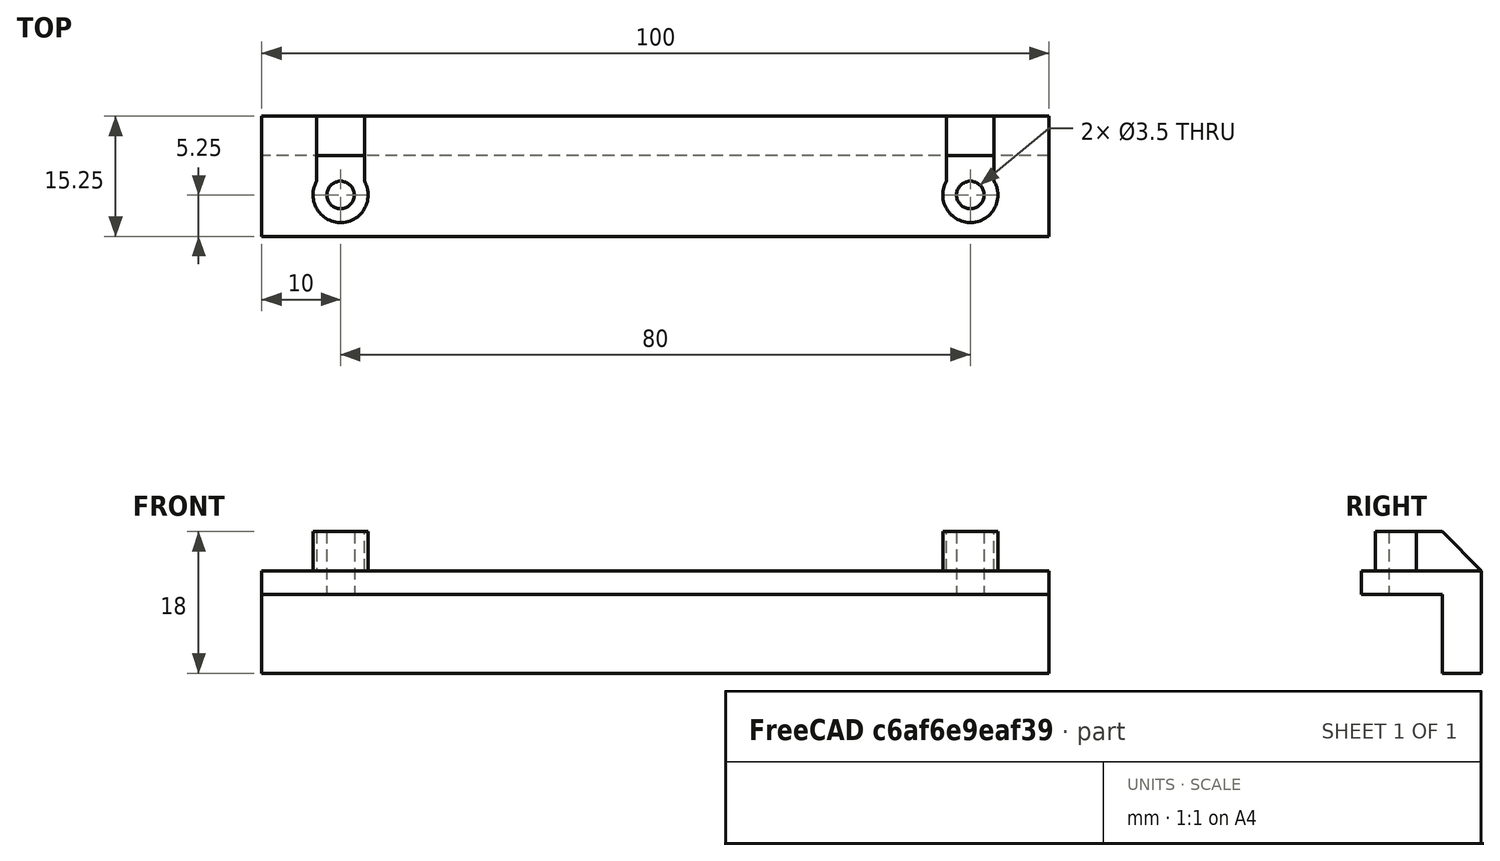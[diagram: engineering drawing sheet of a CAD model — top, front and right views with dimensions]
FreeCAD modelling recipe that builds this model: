
FCSTD DOCUMENT  (FreeCAD 0.19R24276 (Git))
Label: hole_jig
License: All rights reserved
LicenseURL: http://en.wikipedia.org/wiki/All_rights_reserved
objects: TechDraw::DrawProjGroupItem×9, TechDraw::DrawViewDimension×8, Sketcher::SketchObject×4, PartDesign::Pad×4, Spreadsheet::Sheet×1, PartDesign::Chamfer×1, PartDesign::Body×1, TechDraw::DrawSVGTemplate×1, TechDraw::DrawProjGroup×1, TechDraw::DrawPage×1
note: 15 computed .brp shape members not serialized (recipe doc carries the construction recipe); baked Part::Feature solids carry a one-line shape summary decoded from their .brp

FEATURE [Spreadsheet::Sheet] Spreadsheet  label="parameters"
  cells = A1=table_thickness; B1(table_thickness)=10; A2=gap; B2(gap)=0.25; A3=hole_separation; B3(hole_separation)=80; A4=hole_height; B4(hole_height)=5; A5=hole_diameter; B5(hole_diameter)=3; A6=jig_top_thickness; B6(jig_top_thickness)=3; A7=jig_side_thickness; B7(jig_side_thickness)=5; A8=wall; B8(wall)=2
FEATURE [Sketcher::SketchObject] Sketch
  FullyConstrained = true
  MapMode = 5
  Support = -> [XY_Plane]
  expr: Constraints[12] = <<parameters>>.hole_separation / 2
  expr: Constraints[13] = <<parameters>>.table_thickness / 2 + <<parameters>>.gap
  expr: Constraints[7] = <<parameters>>.table_thickness + <<parameters>>.gap + <<parameters>>.jig_side_thickness
  expr: Constraints[8] = <<parameters>>.hole_separation + <<parameters>>.table_thickness * 2
  expr: Constraints[11] = <<parameters>>.hole_separation / 2
  expr: Constraints[9] = <<parameters>>.hole_diameter / 2 + <<parameters>>.gap
  sketch-geometry (6):
    g0: LineSegment StartX=-50 StartY=0 StartZ=0 EndX=50 EndY=0 EndZ=0
    g1: LineSegment StartX=50 StartY=0 StartZ=0 EndX=50 EndY=-15.25 EndZ=0
    g2: LineSegment StartX=50 StartY=-15.25 StartZ=0 EndX=-50 EndY=-15.25 EndZ=0
    g3: LineSegment StartX=-50 StartY=-15.25 StartZ=0 EndX=-50 EndY=0 EndZ=0
    g4: Circle CenterX=-40 CenterY=-10 CenterZ=0 NormalX=0 NormalY=0 NormalZ=1 AngleXU=0 Radius=1.75
    g5: Circle CenterX=40 CenterY=-10 CenterZ=0 NormalX=0 NormalY=0 NormalZ=1 AngleXU=0 Radius=1.75
  constraints (17):
    c: Coincident(g0,g1)
    c: Coincident(g1,g2)
    c: Coincident(g2,g3)
    c: Coincident(g3,g0)
    c: Horizontal(g0)
    c: Vertical(g1)
    c: Vertical(g3)
    c: DistanceY(g1,g1) = 15.25
    c: DistanceX(g0,g0) = 100
    c: Radius(g4) = 1.75
    c: Equal(g4,g5)
    c: DistanceX(g4,g-1) = 40
    c: DistanceX(g-1,g5) = 40
    c: DistanceY(g2,g4) = 5.25
    c: Horizontal(g5,g4)
    c: Symmetric(g2,g1,g-2)
    c: PointOnObject(g0,g-1)
FEATURE [PartDesign::Pad] Pad
  Direction = (1,1,1)
  Length = 3
  Length2 = 100
  Profile = -> Sketch
  Type = 0
  expr: Length = <<parameters>>.jig_top_thickness
FEATURE [Sketcher::SketchObject] Sketch001
  ExternalGeometry = -> [Pad]
  FullyConstrained = true
  MapMode = 5
  Placement = pos=(0,0,0) rot=(1,0,0;3.14159rad)
  Support = -> [Pad]
  expr: Constraints[10] = <<parameters>>.jig_side_thickness
  sketch-geometry (4):
    g0: LineSegment StartX=-50 StartY=0 StartZ=0 EndX=50 EndY=0 EndZ=0
    g1: LineSegment StartX=50 StartY=0 StartZ=0 EndX=50 EndY=5 EndZ=0
    g2: LineSegment StartX=50 StartY=5 StartZ=0 EndX=-50 EndY=5 EndZ=0
    g3: LineSegment StartX=-50 StartY=5 StartZ=0 EndX=-50 EndY=0 EndZ=0
  constraints (11):
    c: Coincident(g0,g1)
    c: Coincident(g1,g2)
    c: Coincident(g2,g3)
    c: Coincident(g3,g0)
    c: Horizontal(g0)
    c: Horizontal(g2)
    c: Vertical(g1)
    c: Vertical(g3)
    c: Coincident(g0,g-3)
    c: PointOnObject(g1,g-4)
    c: DistanceY(g1,g1) = 5
FEATURE [PartDesign::Pad] Pad001
  BaseFeature = -> Pad
  Direction = (1,1,1)
  Length = 10
  Length2 = 100
  Profile = -> Sketch001
  Type = 0
  expr: Length = <<parameters>>.jig_side_thickness * 2
FEATURE [Sketcher::SketchObject] Sketch002
  ExternalGeometry = -> [Pad001]
  FullyConstrained = true
  MapMode = 5
  Placement = pos=(0,0,3) rot=(0,0,1;0rad)
  Support = -> [Pad001]
  expr: Constraints[4] = <<parameters>>.hole_diameter / 2 + <<parameters>>.gap
  expr: Constraints[6] = <<parameters>>.hole_diameter / 2 + <<parameters>>.wall
  sketch-geometry (4):
    g0: Circle CenterX=-40 CenterY=-10 CenterZ=0 NormalX=0 NormalY=0 NormalZ=1 AngleXU=0 Radius=1.75
    g1: Circle CenterX=-40 CenterY=-10 CenterZ=0 NormalX=0 NormalY=0 NormalZ=1 AngleXU=0 Radius=3.5
    g2: Circle CenterX=40 CenterY=-10 CenterZ=0 NormalX=0 NormalY=0 NormalZ=1 AngleXU=0 Radius=1.75
    g3: Circle CenterX=40 CenterY=-10 CenterZ=0 NormalX=0 NormalY=0 NormalZ=1 AngleXU=0 Radius=3.5
  constraints (8):
    c: Coincident(g0,g-3)
    c: Coincident(g1,g0)
    c: Coincident(g2,g-4)
    c: Coincident(g3,g2)
    c: Radius(g0) = 1.75
    c: Equal(g0,g2)
    c: Radius(g1) = 3.5
    c: Equal(g1,g3)
FEATURE [PartDesign::Pad] Pad002
  BaseFeature = -> Pad001
  Direction = (1,1,1)
  Length = 5
  Length2 = 100
  Profile = -> Sketch002
  Type = 0
  expr: Length = <<parameters>>.hole_height
FEATURE [Sketcher::SketchObject] Sketch003
  ExternalGeometry = -> [Pad002]
  FullyConstrained = true
  MapMode = 5
  Placement = pos=(0,0,8) rot=(0,0,1;0rad)
  Support = -> [Pad002]
  sketch-geometry (8):
    g0: LineSegment StartX=-43.0311 StartY=0 StartZ=0 EndX=-36.9689 EndY=0 EndZ=0
    g1: LineSegment StartX=-36.9689 StartY=0 StartZ=0 EndX=-36.9689 EndY=-8.25 EndZ=0
    g2: LineSegment StartX=-36.9689 StartY=-8.25 StartZ=0 EndX=-43.0311 EndY=-8.25 EndZ=0
    g3: LineSegment StartX=-43.0311 StartY=-8.25 StartZ=0 EndX=-43.0311 EndY=0 EndZ=0
    g4: LineSegment StartX=36.9689 StartY=0 StartZ=0 EndX=43.0311 EndY=0 EndZ=0
    g5: LineSegment StartX=43.0311 StartY=0 StartZ=0 EndX=43.0311 EndY=-8.25 EndZ=0
    g6: LineSegment StartX=43.0311 StartY=-8.25 StartZ=0 EndX=36.9689 EndY=-8.25 EndZ=0
    g7: LineSegment StartX=36.9689 StartY=-8.25 StartZ=0 EndX=36.9689 EndY=0 EndZ=0
  constraints (24):
    c: Coincident(g0,g1)
    c: Coincident(g1,g2)
    c: Coincident(g2,g3)
    c: Coincident(g3,g0)
    c: Horizontal(g0)
    c: Horizontal(g2)
    c: Vertical(g1)
    c: Vertical(g3)
    c: PointOnObject(g0,g-3)
    c: PointOnObject(g1,g-4)
    c: Coincident(g4,g5)
    c: Coincident(g5,g6)
    c: Coincident(g6,g7)
    c: Coincident(g7,g4)
    c: Horizontal(g4)
    c: Horizontal(g6)
    c: Vertical(g5)
    c: Vertical(g7)
    c: PointOnObject(g4,g-3)
    c: PointOnObject(g5,g-6)
    c: PointOnObject(g6,g-6)
    c: Tangent(g6,g-7)
    c: PointOnObject(g2,g-4)
    c: Tangent(g2,g-5)
FEATURE [PartDesign::Pad] Pad003
  BaseFeature = -> Pad002
  Direction = (1,1,1)
  Length = 5
  Length2 = 100
  Profile = -> Sketch003
  Refine = true
  Reversed = true
  Type = 0
  expr: Length = <<parameters>>.hole_height
FEATURE [PartDesign::Chamfer] Chamfer
  Angle = 45
  Base = -> Pad003 [Edge41,Edge42]
  BaseFeature = -> Pad003
  ChamferType = 0
  FlipDirection = false
  Size = 5
  Size2 = 1
  SupportTransform = false
  expr: Size = <<parameters>>.hole_height
FEATURE [PartDesign::Body] Body
  Group = -> [Sketch,Pad,Sketch001,Pad001,Sketch002,Pad002,Sketch003,Pad003,Chamfer]
  Origin = -> Origin
  Tip = -> Chamfer
FEATURE [TechDraw::DrawSVGTemplate] Template_Chamfer
  Height = 210
  Orientation = 1
  Width = 297
FEATURE [TechDraw::DrawProjGroupItem] ProjItem  label="Front"
  CoarseView = false
  Direction = (0,-1,0)
  Focus = 100
  HardHidden = false
  IsoCount = 0
  IsoHidden = false
  IsoVisible = false
  LockPosition = true
  Perspective = false
  Rotation = 0
  RotationVector = (1,0,0)
  Scale = 0.5
  ScaleType = 2
  SeamHidden = false
  SeamVisible = true
  SmoothHidden = false
  SmoothVisible = true
  Source = -> [Chamfer]
  Type = 0
  X = 0
  XDirection = (1,0,0)
  Y = 0
FEATURE [TechDraw::DrawProjGroupItem] ProjItem001  label="Right"
  CoarseView = false
  Direction = (1,-1e-16,0)
  Focus = 100
  HardHidden = false
  IsoCount = 0
  IsoHidden = false
  IsoVisible = false
  LockPosition = false
  Perspective = false
  Rotation = 0
  RotationVector = (1,0,0)
  Scale = 0.5
  ScaleType = 2
  SeamHidden = false
  SeamVisible = true
  SmoothHidden = false
  SmoothVisible = true
  Source = -> [Chamfer]
  Type = 2
  X = -43.8125
  XDirection = (1e-16,1,0)
  Y = 0
FEATURE [TechDraw::DrawProjGroupItem] ProjItem002  label="Top"
  CoarseView = false
  Direction = (0,0,1)
  Focus = 100
  HardHidden = false
  IsoCount = 0
  IsoHidden = false
  IsoVisible = false
  LockPosition = false
  Perspective = false
  Rotation = 0
  RotationVector = (1,0,0)
  Scale = 0.5
  ScaleType = 2
  SeamHidden = false
  SeamVisible = true
  SmoothHidden = false
  SmoothVisible = true
  Source = -> [Chamfer]
  Type = 4
  X = 0
  XDirection = (1,0,0)
  Y = -86.1875
FEATURE [TechDraw::DrawProjGroupItem] ProjItem003  label="Left"
  CoarseView = false
  Direction = (-1,-1e-16,0)
  Focus = 100
  HardHidden = false
  IsoCount = 0
  IsoHidden = false
  IsoVisible = false
  LockPosition = false
  Perspective = false
  Rotation = 0
  RotationVector = (1,0,0)
  Scale = 0.5
  ScaleType = 2
  SeamHidden = false
  SeamVisible = true
  SmoothHidden = false
  SmoothVisible = true
  Source = -> [Chamfer]
  Type = 1
  X = 43.8125
  XDirection = (1e-16,-1,0)
  Y = 0
FEATURE [TechDraw::DrawProjGroupItem] ProjItem004  label="Bottom"
  CoarseView = false
  Direction = (0,0,-1)
  Focus = 100
  HardHidden = false
  IsoCount = 0
  IsoHidden = false
  IsoVisible = false
  LockPosition = false
  Perspective = false
  Rotation = 0
  RotationVector = (1,0,0)
  Scale = 0.5
  ScaleType = 2
  SeamHidden = false
  SeamVisible = true
  SmoothHidden = false
  SmoothVisible = true
  Source = -> [Chamfer]
  Type = 5
  X = 0
  XDirection = (1,0,0)
  Y = 43.8125
FEATURE [TechDraw::DrawProjGroupItem] ProjItem005  label="FrontBottomLeft"
  CoarseView = false
  Direction = (-0.57735,-0.57735,-0.57735)
  Focus = 100
  HardHidden = false
  IsoCount = 0
  IsoHidden = false
  IsoVisible = false
  LockPosition = false
  Perspective = false
  Rotation = 0
  RotationVector = (1,0,0)
  Scale = 0.5
  ScaleType = 2
  SeamHidden = false
  SeamVisible = true
  SmoothHidden = false
  SmoothVisible = true
  Source = -> [Chamfer]
  Type = 8
  X = 60.3735
  XDirection = (0.707107,-0.707107,0)
  Y = 54.4163
FEATURE [TechDraw::DrawProjGroupItem] ProjItem006  label="FrontTopRight"
  CoarseView = false
  Direction = (0.57735,-0.57735,0.57735)
  Focus = 100
  HardHidden = false
  IsoCount = 0
  IsoHidden = false
  IsoVisible = false
  LockPosition = false
  Perspective = false
  Rotation = 0
  RotationVector = (1,0,0)
  Scale = 0.5
  ScaleType = 2
  SeamHidden = false
  SeamVisible = true
  SmoothHidden = false
  SmoothVisible = true
  Source = -> [Chamfer]
  Type = 7
  X = -60.3735
  XDirection = (0.707107,0.707107,0)
  Y = -76.6299
FEATURE [TechDraw::DrawProjGroupItem] ProjItem007  label="FrontTopLeft"
  CoarseView = false
  Direction = (-0.57735,-0.57735,0.57735)
  Focus = 100
  HardHidden = false
  IsoCount = 0
  IsoHidden = false
  IsoVisible = false
  LockPosition = false
  Perspective = false
  Rotation = 0
  RotationVector = (1,0,0)
  Scale = 0.5
  ScaleType = 2
  SeamHidden = false
  SeamVisible = true
  SmoothHidden = false
  SmoothVisible = true
  Source = -> [Chamfer]
  Type = 6
  X = 60.3735
  XDirection = (0.707107,-0.707107,0)
  Y = -76.6299
FEATURE [TechDraw::DrawProjGroupItem] ProjItem008  label="FrontBottomRight"
  CoarseView = false
  Direction = (0.57735,-0.57735,-0.57735)
  Focus = 100
  HardHidden = false
  IsoCount = 0
  IsoHidden = false
  IsoVisible = false
  LockPosition = false
  Perspective = false
  Rotation = 0
  RotationVector = (1,0,0)
  Scale = 0.5
  ScaleType = 2
  SeamHidden = false
  SeamVisible = true
  SmoothHidden = false
  SmoothVisible = true
  Source = -> [Chamfer]
  Type = 9
  X = -60.3735
  XDirection = (0.707107,0.707107,0)
  Y = 54.4163
FEATURE [TechDraw::DrawProjGroup] ProjGroup_Chamfer
  Anchor = -> ProjItem
  AutoDistribute = true
  LockPosition = false
  ProjectionType = 0
  Rotation = 0
  Scale = 0.5
  ScaleType = 1
  Source = -> [Chamfer]
  Views = -> [ProjItem,ProjItem001,ProjItem002,ProjItem003,ProjItem004,ProjItem005,ProjItem006,ProjItem007,ProjItem008]
  X = 148.5
  Y = 105
  spacingX = 15
  spacingY = 15
FEATURE [TechDraw::DrawViewDimension] Dimension
  Arbitrary = false
  ArbitraryTolerances = false
  EqualTolerance = true
  FormatSpec = %.2f
  FormatSpecOverTolerance = %+.2f
  FormatSpecUnderTolerance = %+.2f
  Inverted = false
  LockPosition = false
  MeasureType = 1
  OverTolerance = 0
  References2D = -> [ProjItem004]
  Rotation = 0
  ScaleType = 0
  TheoreticalExact = false
  Type = 1
  UnderTolerance = 0
  X = -0.369264
  Y = 22.0911
FEATURE [TechDraw::DrawViewDimension] Dimension001
  Arbitrary = false
  ArbitraryTolerances = false
  EqualTolerance = true
  FormatSpec = %.2f
  FormatSpecOverTolerance = %+.2f
  FormatSpecUnderTolerance = %+.2f
  Inverted = false
  LockPosition = false
  MeasureType = 1
  OverTolerance = 0
  References2D = -> [ProjItem004]
  Rotation = 0
  ScaleType = 0
  TheoreticalExact = false
  Type = 2
  UnderTolerance = 0
  X = 31.0929
  Y = 18.6054
FEATURE [TechDraw::DrawViewDimension] Dimension002
  Arbitrary = false
  ArbitraryTolerances = false
  EqualTolerance = true
  FormatSpec = %.2f
  FormatSpecOverTolerance = %+.2f
  FormatSpecUnderTolerance = %+.2f
  Inverted = false
  LockPosition = false
  MeasureType = 1
  OverTolerance = 0
  References2D = -> [ProjItem004]
  Rotation = 0
  ScaleType = 0
  TheoreticalExact = false
  Type = 2
  UnderTolerance = 0
  X = -33.8623
  Y = -20.2872
FEATURE [TechDraw::DrawViewDimension] Dimension003
  Arbitrary = false
  ArbitraryTolerances = false
  EqualTolerance = true
  FormatSpec = %.2f
  FormatSpecOverTolerance = %+.2f
  FormatSpecUnderTolerance = %+.2f
  Inverted = false
  LockPosition = false
  MeasureType = 1
  OverTolerance = 0
  References2D = -> [ProjItem004]
  Rotation = 0
  ScaleType = 0
  TheoreticalExact = false
  Type = 1
  UnderTolerance = 0
  X = -0.971319
  Y = 15.0349
FEATURE [TechDraw::DrawViewDimension] Dimension004
  Arbitrary = false
  ArbitraryTolerances = false
  EqualTolerance = true
  FormatSpec = R%.2f
  FormatSpecOverTolerance = %+.2f
  FormatSpecUnderTolerance = %+.2f
  Inverted = false
  LockPosition = false
  MeasureType = 1
  OverTolerance = 0
  References2D = -> [ProjItem004]
  Rotation = 0
  ScaleType = 0
  TheoreticalExact = false
  Type = 4
  UnderTolerance = 0
  X = 15.6937
  Y = -9.41623
FEATURE [TechDraw::DrawViewDimension] Dimension005
  Arbitrary = false
  ArbitraryTolerances = false
  EqualTolerance = true
  FormatSpec = %.2f
  FormatSpecOverTolerance = %+.2f
  FormatSpecUnderTolerance = %+.2f
  Inverted = false
  LockPosition = false
  MeasureType = 1
  OverTolerance = 0
  References2D = -> [ProjItem003]
  Rotation = 0
  ScaleType = 0
  TheoreticalExact = false
  Type = 2
  UnderTolerance = 0
  X = 13.4615
  Y = 15.0664
FEATURE [TechDraw::DrawViewDimension] Dimension006
  Arbitrary = false
  ArbitraryTolerances = false
  EqualTolerance = true
  FormatSpec = %.2f
  FormatSpecOverTolerance = %+.2f
  FormatSpecUnderTolerance = %+.2f
  Inverted = false
  LockPosition = false
  MeasureType = 1
  OverTolerance = 0
  References2D = -> [ProjItem003]
  Rotation = 0
  ScaleType = 0
  TheoreticalExact = false
  Type = 1
  UnderTolerance = 0
  X = 26.5446
  Y = -15.0091
FEATURE [TechDraw::DrawViewDimension] Dimension007
  Arbitrary = false
  ArbitraryTolerances = false
  EqualTolerance = true
  FormatSpec = %.2f
  FormatSpecOverTolerance = %+.2f
  FormatSpecUnderTolerance = %+.2f
  Inverted = false
  LockPosition = false
  MeasureType = 1
  OverTolerance = 0
  References2D = -> [ProjItem003]
  Rotation = 0
  ScaleType = 0
  TheoreticalExact = false
  Type = 2
  UnderTolerance = 0
  X = -11.3824
  Y = 19.798
FEATURE [TechDraw::DrawPage] Page_Chamfer
  KeepUpdated = true
  NextBalloonIndex = 1
  ProjectionType = 0
  Template = -> Template_Chamfer
  Views = -> [ProjGroup_Chamfer,Dimension,Dimension001,Dimension002,Dimension003,Dimension004,Dimension005,Dimension006,Dimension007]
